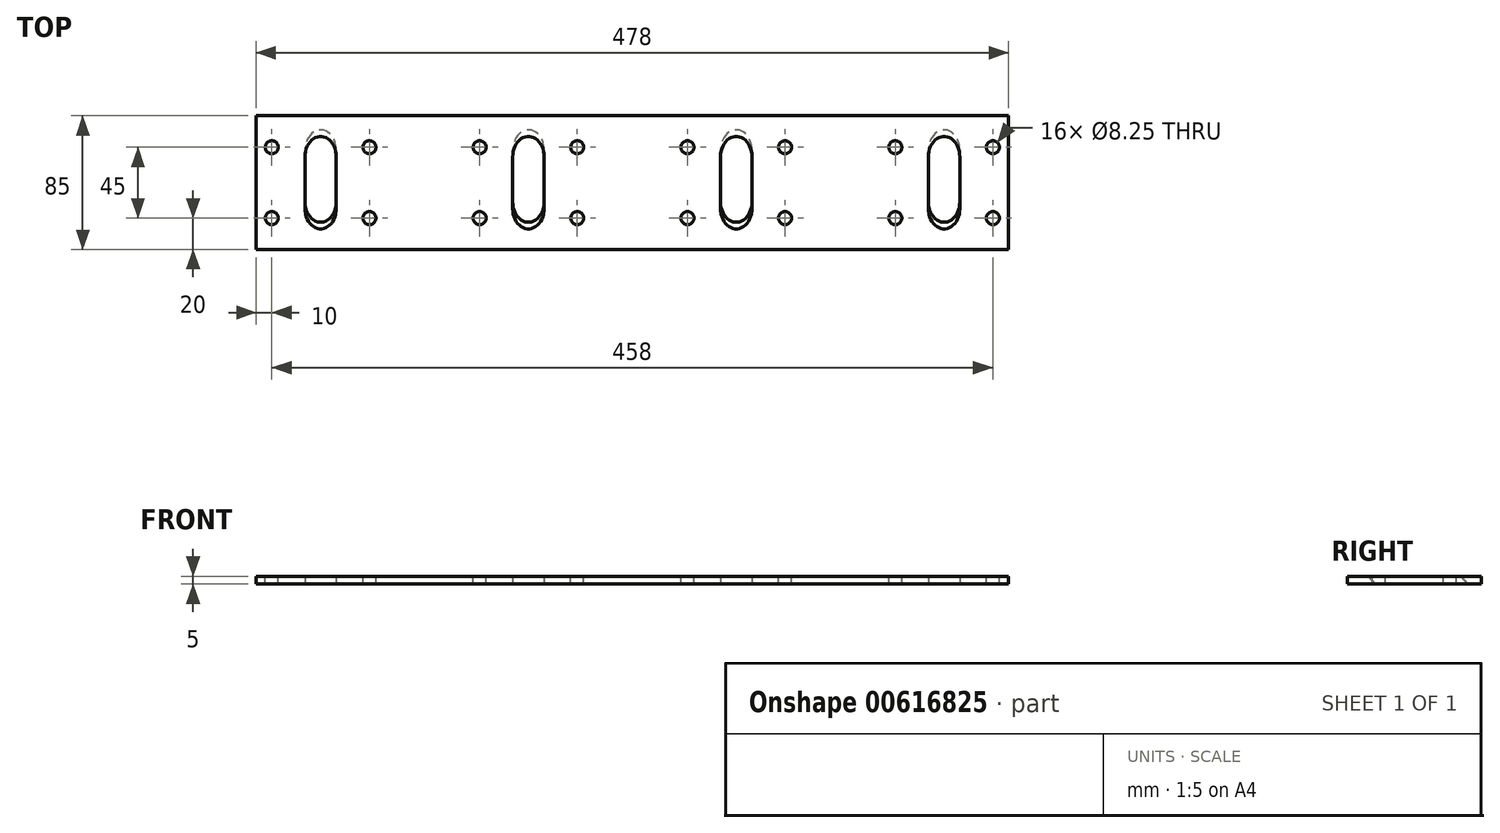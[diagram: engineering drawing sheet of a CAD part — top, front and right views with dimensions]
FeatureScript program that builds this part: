
annotation { "Feature Type Name" : "Feature", "Feature Type Description" : "" }
export const myFeature = defineFeature(function(context is Context, id is Id, definition is map)
    precondition{}
    {
        {
            var Q0;
            Q0=qCreatedBy(makeId("Top.planeOp"),FACE);
            var sketch = newSketch(context, id + "F0", { "sketchPlane" : qUnion([Q0])});
            skLineSegment(sketch, "E0.bottom", {"start": v(239, 42.5) * mm, "end": v(-239, 42.5) * mm});
            skLineSegment(sketch, "E0.top", {"start": v(239, -42.5) * mm, "end": v(-239, -42.5) * mm});
            skLineSegment(sketch, "E0.left", {"start": v(239, 42.5) * mm, "end": v(239, -42.5) * mm});
            skLineSegment(sketch, "E0.right", {"start": v(-239, 42.5) * mm, "end": v(-239, -42.5) * mm});
            skPoint(sketch, "E0.middle", {"position": v(0, 0) * mm});
            skPoint(sketch, "E1", {"position": v(-229, -22.5) * mm});
            skPoint(sketch, "E2", {"position": v(-229, 22.5) * mm});
            skPoint(sketch, "E3.1.0.0", {"position": v(-167, 22.5) * mm});
            skPoint(sketch, "E3.1.0.1", {"position": v(-167, -22.5) * mm});
            skLineSegment(sketch, "E3.direction1", {"start": v(-229, 22.5) * mm, "end": v(-167, 22.5) * mm, "construction": true});
            skPoint(sketch, "E4.1.0.0", {"position": v(-97, 22.5) * mm});
            skPoint(sketch, "E4.1.0.1", {"position": v(-97, -22.5) * mm});
            skPoint(sketch, "E4.1.0.2", {"position": v(-35, 22.5) * mm});
            skPoint(sketch, "E4.1.0.3", {"position": v(-35, -22.5) * mm});
            skPoint(sketch, "E4.2.0.0", {"position": v(35, 22.5) * mm});
            skPoint(sketch, "E4.2.0.1", {"position": v(35, -22.5) * mm});
            skPoint(sketch, "E4.2.0.2", {"position": v(97, 22.5) * mm});
            skPoint(sketch, "E4.2.0.3", {"position": v(97, -22.5) * mm});
            skLineSegment(sketch, "E4.direction1", {"start": v(-229, 22.5) * mm, "end": v(-97, 22.5) * mm, "construction": true});
            skPoint(sketch, "E5.0.3.0", {"position": v(167, 22.5) * mm});
            skPoint(sketch, "E5.1.3.0", {"position": v(167, -22.5) * mm});
            skPoint(sketch, "E5.2.3.0", {"position": v(229, 22.5) * mm});
            skPoint(sketch, "E5.3.3.0", {"position": v(229, -22.5) * mm});
            skSolve(sketch);
        }
        {
            var Q0;
            Q0 = qSketchRegion(id + "F0", true);
            extrude(context, id + "F1", {"entities" : qUnion([Q0]), "depth" : 5 * mm, "offsetDistance" : 25 * mm});
        }
        {
            var Q0;
            Q0=sQuery(id+"F0.wireOp",VERTEX,"E2");
            var Q1;
            Q1=sQuery(id+"F0.wireOp",VERTEX,"E1");
            var Q2;
            Q2=sQuery(id+"F0.wireOp",VERTEX,"E3.1.0.0");
            var Q3;
            Q3=sQuery(id+"F0.wireOp",VERTEX,"E3.1.0.1");
            var Q4;
            Q4=sQuery(id+"F0.wireOp",VERTEX,"E4.1.0.0");
            var Q5;
            Q5=sQuery(id+"F0.wireOp",VERTEX,"E4.1.0.1");
            var Q6;
            Q6=sQuery(id+"F0.wireOp",VERTEX,"E4.1.0.2");
            var Q7;
            Q7=sQuery(id+"F0.wireOp",VERTEX,"E4.1.0.3");
            var Q8;
            Q8=sQuery(id+"F0.wireOp",VERTEX,"E4.2.0.0");
            var Q9;
            Q9=sQuery(id+"F0.wireOp",VERTEX,"E4.2.0.1");
            var Q10;
            Q10=sQuery(id+"F0.wireOp",VERTEX,"E4.2.0.2");
            var Q11;
            Q11=sQuery(id+"F0.wireOp",VERTEX,"E4.2.0.3");
            var Q12;
            Q12=sQuery(id+"F0.wireOp",VERTEX,"E5.0.3.0");
            var Q13;
            Q13=sQuery(id+"F0.wireOp",VERTEX,"E5.1.3.0");
            var Q14;
            Q14=sQuery(id+"F0.wireOp",VERTEX,"E5.2.3.0");
            var Q15;
            Q15=sQuery(id+"F0.wireOp",VERTEX,"E5.3.3.0");
            var Q16;
            Q16=makeQuery(id+"F1.opExtrude","SWEPT_BODY",BODY,{"disambiguationData":[OSD([sQuery(id+"F0.wireOp",EDGE,"E0.bottom"),sQuery(id+"F0.wireOp",EDGE,"E0.top"),sQuery(id+"F0.wireOp",EDGE,"E0.left"),sQuery(id+"F0.wireOp",EDGE,"E0.right")])]});
            hole(context, id + "F2", {"style" : HoleStyle.SIMPLE, "endStyle" : HoleEndStyle.THROUGH, "oppositeDirection" : true, "holeDiameter" : 8.25 * mm, "majorDiameter" : 12 * mm, "isTappedThrough" : true, "tappedDepth" : 12 * mm, "tapClearance" : 3, "locations" : qUnion([Q0, Q1, Q2, Q3, Q4, Q5, Q6, Q7, Q8, Q9, Q10, Q11, Q12, Q13, Q14, Q15]), "scope" : qUnion([Q16]), "startStyle" : HoleStartStyle.PART});
        }
        {
            var Q0;
            Q0=makeQuery(id+"F1.opExtrude","CAP_EDGE",EDGE,{"disambiguationData":[OSD([sQuery(id+"F0.wireOp",EDGE,"E0.bottom")])],"isStart":false});
            cPlane(context, id + "F3", {"entities" : qUnion([Q0]), "cplaneType" : CPlaneType.LINE_ANGLE, "offset" : 25 * mm, "angle" : 50 * degree, "width" : 150 * mm, "height" : 150 * mm});
        }
        {
            var Q0;
            Q0=qCreatedBy(id+"F3.planeOp",FACE);
            var sketch = newSketch(context, id + "F4", { "sketchPlane" : qUnion([Q0])});
            skLineSegment(sketch, "E6.left", {"start": v(208, -9.28) * mm, "end": v(208, 15.72) * mm});
            skLineSegment(sketch, "E6.right", {"start": v(188, -9.28) * mm, "end": v(188, 15.72) * mm});
            skPoint(sketch, "E6.middle", {"position": v(198, 3.22) * mm});
            skArc(sketch, "E7", {"start": v(208, 15.72) * mm, "mid": v(198, 25.72) * mm, "end": v(188, 15.72) * mm});
            skArc(sketch, "E8", {"start": v(188, -9.28) * mm, "mid": v(198, -19.28) * mm, "end": v(208, -9.28) * mm});
            skLineSegment(sketch, "E9.1.0.0", {"start": v(56, -9.28) * mm, "end": v(56, 15.72) * mm});
            skArc(sketch, "E9.1.0.1", {"start": v(56, -9.28) * mm, "mid": v(66, -19.28) * mm, "end": v(76, -9.28) * mm});
            skLineSegment(sketch, "E9.1.0.2", {"start": v(76, -9.28) * mm, "end": v(76, 15.72) * mm});
            skArc(sketch, "E9.1.0.3", {"start": v(76, 15.72) * mm, "mid": v(66, 25.72) * mm, "end": v(56, 15.72) * mm});
            skLineSegment(sketch, "E9.2.0.0", {"start": v(-76, -9.28) * mm, "end": v(-76, 15.72) * mm});
            skArc(sketch, "E9.2.0.1", {"start": v(-76, -9.28) * mm, "mid": v(-66, -19.28) * mm, "end": v(-56, -9.28) * mm});
            skLineSegment(sketch, "E9.2.0.2", {"start": v(-56, -9.28) * mm, "end": v(-56, 15.72) * mm});
            skArc(sketch, "E9.2.0.3", {"start": v(-56, 15.72) * mm, "mid": v(-66, 25.72) * mm, "end": v(-76, 15.72) * mm});
            skLineSegment(sketch, "E9.3.0.0", {"start": v(-208, -9.28) * mm, "end": v(-208, 15.72) * mm});
            skArc(sketch, "E9.3.0.1", {"start": v(-208, -9.28) * mm, "mid": v(-198, -19.28) * mm, "end": v(-188, -9.28) * mm});
            skLineSegment(sketch, "E9.3.0.2", {"start": v(-188, -9.28) * mm, "end": v(-188, 15.72) * mm});
            skArc(sketch, "E9.3.0.3", {"start": v(-188, 15.72) * mm, "mid": v(-198, 25.72) * mm, "end": v(-208, 15.72) * mm});
            skLineSegment(sketch, "E9.direction1", {"start": v(188, -9.28) * mm, "end": v(56, -9.28) * mm, "construction": true});
            skSolve(sketch);
        }
        {
            var Q0;
            Q0 = qSketchRegion(id + "F4", true);
            extrude(context, id + "F5", {"entities" : qUnion([Q0]), "operationType" : NewBodyOperationType.REMOVE, "endBound" : BoundingType.THROUGH_ALL, "depth" : 25 * mm, "offsetDistance" : 25 * mm});
        }
    });
